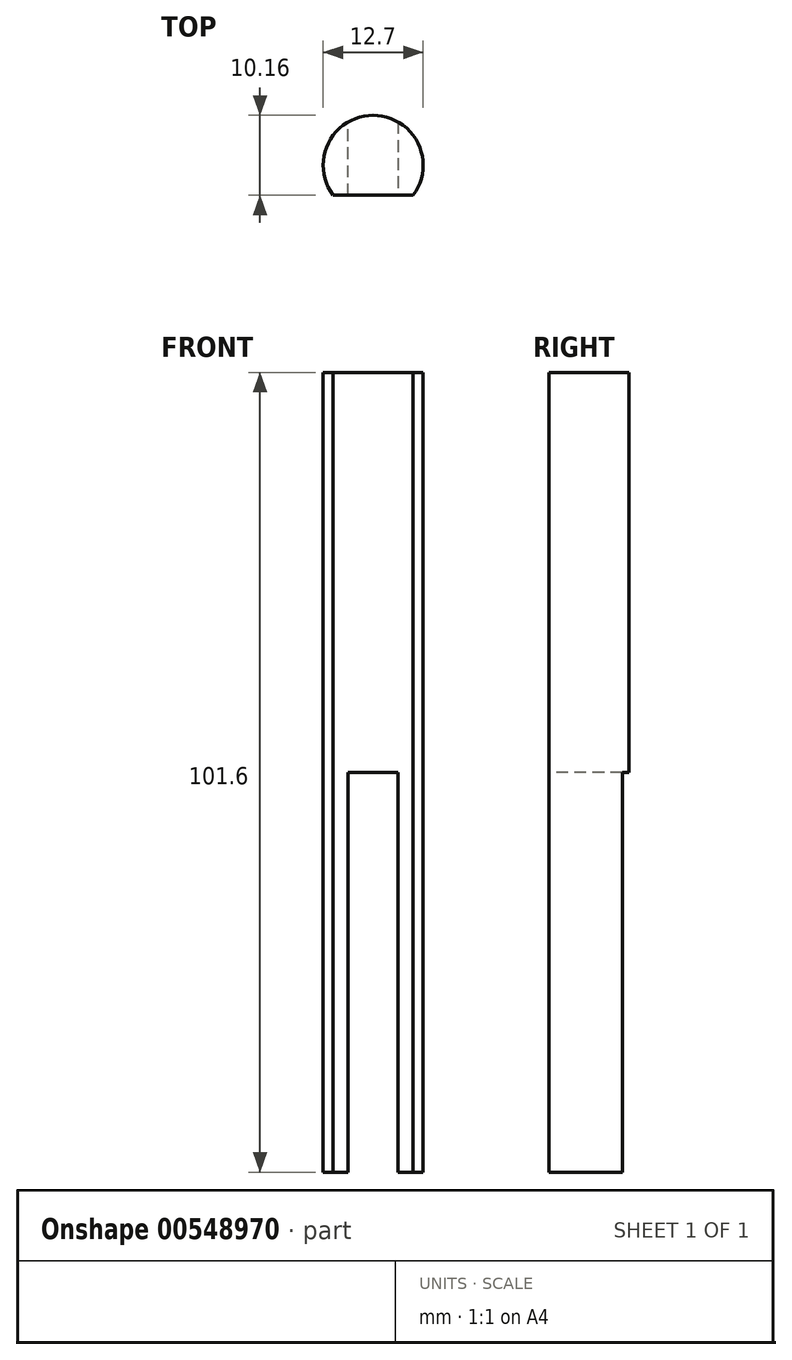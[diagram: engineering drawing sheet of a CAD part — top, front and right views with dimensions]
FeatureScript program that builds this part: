
annotation { "Feature Type Name" : "Feature", "Feature Type Description" : "" }
export const myFeature = defineFeature(function(context is Context, id is Id, definition is map)
    precondition{}
    {
        {
            var Q0;
            Q0=qCreatedBy(makeId("Top.planeOp"),FACE);
            var sketch = newSketch(context, id + "F0", { "sketchPlane" : qUnion([Q0])});
            skArc(sketch, "E0", {"start": v(5.08, -3.81) * mm, "mid": v(0, 6.35) * mm, "end": v(-5.08, -3.81) * mm});
            skLineSegment(sketch, "E1", {"start": v(-3.18, -3.8) * mm, "end": v(-3.18, 5.5) * mm});
            skLineSegment(sketch, "E2", {"start": v(3.17, 5.5) * mm, "end": v(3.18, -3.8) * mm});
            skLineSegment(sketch, "E3", {"start": v(-5.08, -3.8) * mm, "end": v(5.08, -3.8) * mm});
            skSolve(sketch);
        }
        {
            var Q0;
            {var subQ0=sQuery(id+"F0.wireOp",EDGE,"E1");Q0=makeQuery(id+"F0.imprint","IMPRINT",FACE,{"disambiguationData":[TD([[makeQuery(id+"F0.imprint","IMPRINT",EDGE,{"derivedFrom":subQ0}),1.0]])]});}
            var Q1;
            {var subQ0=sQuery(id+"F0.wireOp",EDGE,"E1");Q1=makeQuery(id+"F0.imprint","IMPRINT",FACE,{"disambiguationData":[TD([[makeQuery(id+"F0.imprint","IMPRINT",EDGE,{"derivedFrom":subQ0}),-1.0]])]});}
            var Q2;
            {var subQ0=sQuery(id+"F0.wireOp",EDGE,"E2");Q2=makeQuery(id+"F0.imprint","IMPRINT",FACE,{"disambiguationData":[TD([[makeQuery(id+"F0.imprint","IMPRINT",EDGE,{"derivedFrom":subQ0}),1.0]])]});}
            extrude(context, id + "F1", {"entities" : qUnion([Q0, Q1, Q2]), "depth" : 50.8 * mm, "offsetDistance" : 25.4 * mm});
        }
        {
            var Q0;
            {var subQ0=sQuery(id+"F0.wireOp",EDGE,"E2");Q0=makeQuery(id+"F0.imprint","IMPRINT",FACE,{"disambiguationData":[TD([[makeQuery(id+"F0.imprint","IMPRINT",EDGE,{"derivedFrom":subQ0}),1.0]])]});}
            var Q1;
            {var subQ0=sQuery(id+"F0.wireOp",EDGE,"E1");Q1=makeQuery(id+"F0.imprint","IMPRINT",FACE,{"disambiguationData":[TD([[makeQuery(id+"F0.imprint","IMPRINT",EDGE,{"derivedFrom":subQ0}),1.0]])]});}
            extrude(context, id + "F2", {"entities" : qUnion([Q0, Q1]), "operationType" : NewBodyOperationType.ADD, "oppositeDirection" : true, "depth" : 50.8 * mm, "offsetDistance" : 25.4 * mm});
        }
    });
